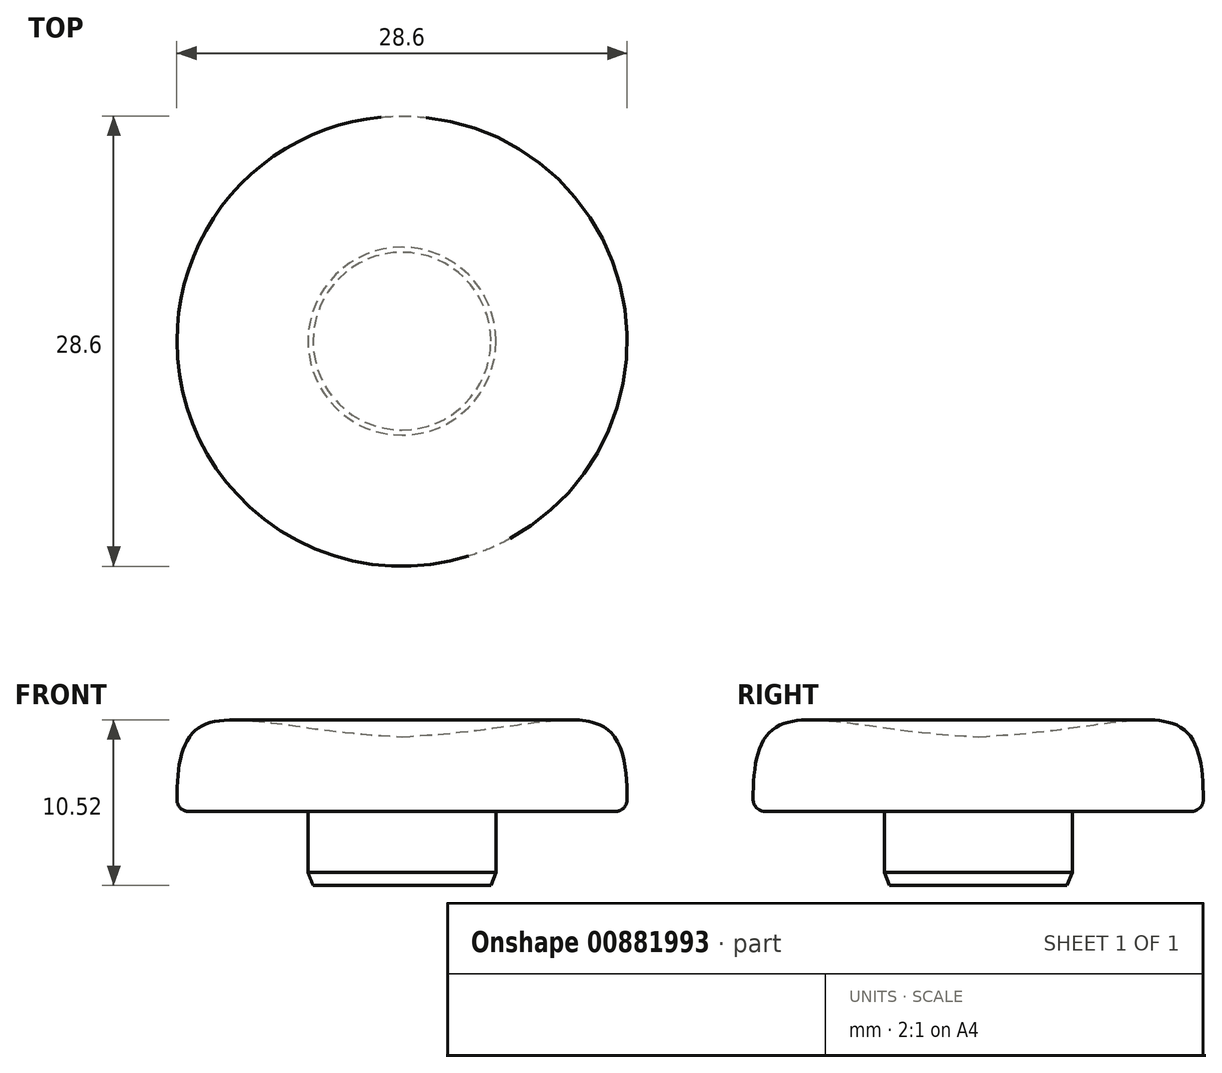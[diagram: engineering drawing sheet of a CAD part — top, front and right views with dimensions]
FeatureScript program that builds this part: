
annotation { "Feature Type Name" : "Feature", "Feature Type Description" : "" }
export const myFeature = defineFeature(function(context is Context, id is Id, definition is map)
    precondition{}
    {
        {
            var Q0;
            Q0=qCreatedBy(makeId("Front.planeOp"),FACE);
            var sketch = newSketch(context, id + "F0", { "sketchPlane" : qUnion([Q0])});
            skLineSegment(sketch, "E0", {"start": v(0, 0) * mm, "end": v(-5.64, 0) * mm});
            skLineSegment(sketch, "E1", {"start": v(-5.97, 0.82) * mm, "end": v(-5.97, 4.7) * mm});
            skLineSegment(sketch, "E2", {"start": v(-5.97, 4.7) * mm, "end": v(-13.53, 4.7) * mm});
            skPoint(sketch, "E3.orphan", {"position": v(0, 4.7) * mm});
            skFitSpline(sketch, "E4", {"points": [v(-14.29, 4.7) * mm, v(-13.16, 9.82) * mm, v(-8.76, 10.4) * mm, v(0, 9.44) * mm], "startDerivative": vector(-0.48, 20.4) * mm, "endDerivative": vector(31.78, -1.71) * mm});
            skLineSegment(sketch, "E5", {"start": v(0, 0) * mm, "end": v(0, 15.7) * mm, "construction": true});
            skLineSegment(sketch, "E6", {"start": v(0, 0) * mm, "end": v(0, 9.44) * mm});
            skArc(sketch, "E7.filletArc", {"start": v(-14.3, 5.46) * mm, "mid": v(-14.07, 4.92) * mm, "end": v(-13.53, 4.7) * mm});
            skLineSegment(sketch, "E8", {"start": v(-5.97, 0.82) * mm, "end": v(-5.64, 0) * mm});
            skSolve(sketch);
        }
        {
            var Q0;
            Q0 = qSketchRegion(id + "F0", true);
            var Q1;
            Q1=sQuery(id+"F0.wireOp",EDGE,"E5");
            revolve(context, id + "F1", {"surfaceOperationType" : NewSurfaceOperationType.NEW, "entities" : qUnion([Q0]), "axis" : qUnion([Q1]), "revolveType" : RevolveType.FULL});
        }
    });
